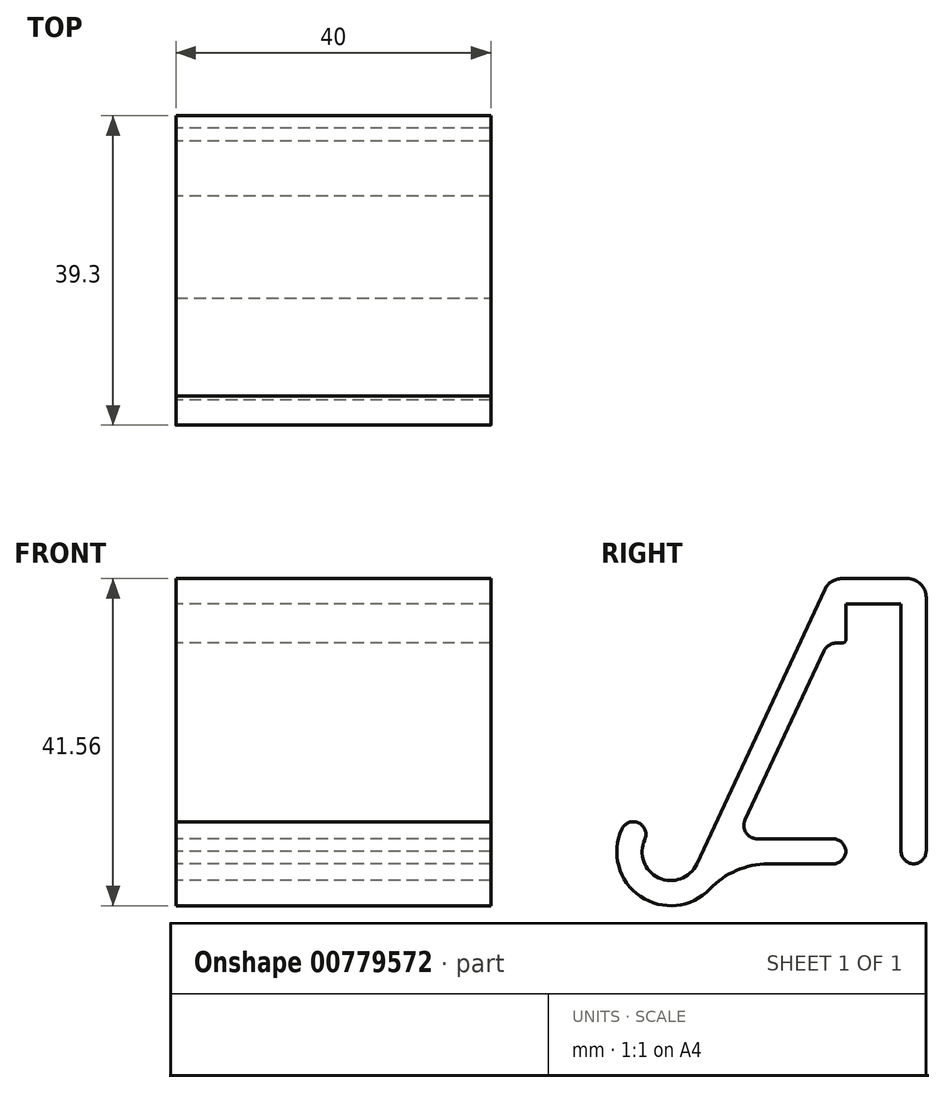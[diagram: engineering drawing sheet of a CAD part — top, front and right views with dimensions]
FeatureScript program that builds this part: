
annotation { "Feature Type Name" : "Feature", "Feature Type Description" : "" }
export const myFeature = defineFeature(function(context is Context, id is Id, definition is map)
    precondition{}
    {
        {
            var Q0;
            Q0=qCreatedBy(makeId("Right.planeOp"),FACE);
            var sketch = newSketch(context, id + "F0", { "sketchPlane" : qUnion([Q0])});
            skLineSegment(sketch, "E0", {"start": v(0, 0) * mm, "end": v(0, 33.05) * mm});
            skLineSegment(sketch, "E1", {"start": v(0, 33.05) * mm, "end": v(7, 33.05) * mm});
            skLineSegment(sketch, "E2", {"start": v(7, 33.05) * mm, "end": v(7, 0) * mm});
            skLineSegment(sketch, "E3", {"start": v(7, 0) * mm, "end": v(10.2, 0) * mm});
            skLineSegment(sketch, "E4", {"start": v(10.2, 0) * mm, "end": v(10.2, 36.25) * mm});
            skLineSegment(sketch, "E5", {"start": v(10.2, 36.25) * mm, "end": v(-2.04, 36.25) * mm});
            skLineSegment(sketch, "E6", {"start": v(-2.04, 36.25) * mm, "end": v(-2.04, 0) * mm, "construction": true});
            skLineSegment(sketch, "E7", {"start": v(-2.04, 0) * mm, "end": v(0, 0) * mm});
            skLineSegment(sketch, "E8", {"start": v(0, 33.05) * mm, "end": v(0, 36.25) * mm, "construction": true});
            skLineSegment(sketch, "E9", {"start": v(-2.04, 0) * mm, "end": v(-18.94, 0) * mm});
            skLineSegment(sketch, "E10", {"start": v(-18.94, 0) * mm, "end": v(-2.04, 36.25) * mm});
            skLineSegment(sketch, "E11", {"start": v(-18.94, 0) * mm, "end": v(-25.56, 3.09) * mm, "construction": true});
            skArc(sketch, "E12", {"start": v(-25.56, 3.09) * mm, "mid": v(-23.8, -1.77) * mm, "end": v(-18.94, 0) * mm});
            skLineSegment(sketch, "E13", {"start": v(-25.56, 3.09) * mm, "end": v(-28.46, 4.44) * mm, "construction": true});
            skCircle(sketch, "E14", {"center": v(-27, 3.76) * mm, "radius": 1.6 * mm});
            skCircle(sketch, "E15", {"center": v(-22.25, 1.54) * mm, "radius": 6.85 * mm});
            skLineSegment(sketch, "E16", {"start": v(-16.04, -1.35) * mm, "end": v(0, 33.05) * mm});
            skLineSegment(sketch, "E17", {"start": v(0, 33.05) * mm, "end": v(0, 33.05) * mm});
            skLineSegment(sketch, "E18", {"start": v(0, 3.2) * mm, "end": v(-17.45, 3.2) * mm});
            skLineSegment(sketch, "E19", {"start": v(-5.37, 3.2) * mm, "end": v(-5.37, 0) * mm, "construction": true});
            skLineSegment(sketch, "E20", {"start": v(0, 28.05) * mm, "end": v(-2.33, 28.05) * mm});
            skSolve(sketch);
        }
        {
            var Q0;
            {var subQ0=sQuery(id+"F0.wireOp",EDGE,"E14");var subQ1=makeQuery(id+"F0.imprint","INTERSECT",VERTEX,{"derivedFrom":[sQuery(id+"F0.wireOp",EDGE,"E12"),subQ0]});Q0=makeQuery(id+"F0.imprint","IMPRINT",FACE,{"disambiguationData":[TD([[makeQuery(id+"F0.imprint","IMPRINT",EDGE,{"disambiguationData":[TD([[subQ1,1.0]])],"derivedFrom":subQ0}),1.0]])]});}
            var Q1;
            {var subQ4=sQuery(id+"F0.wireOp",EDGE,"E12");Q1=makeQuery(id+"F0.imprint","IMPRINT",FACE,{"disambiguationData":[TD([[makeQuery(id+"F0.imprint","IMPRINT",EDGE,{"derivedFrom":subQ4}),-1.0]])]});}
            var Q2;
            {var subQ1=sQuery(id+"F0.wireOp",EDGE,"E9");var subQ3=sQuery(id+"F0.wireOp",EDGE,"E15");var subQ4=makeQuery(id+"F0.imprint","INTERSECT",VERTEX,{"derivedFrom":[subQ1,subQ3]});Q2=makeQuery(id+"F0.imprint","IMPRINT",FACE,{"disambiguationData":[TD([[makeQuery(id+"F0.imprint","IMPRINT",EDGE,{"disambiguationData":[TD([[subQ4,-1.0]])],"derivedFrom":subQ3}),1.0]])]});}
            var Q3;
            {var subQ0=sQuery(id+"F0.wireOp",EDGE,"E16");var subQ1=sQuery(id+"F0.wireOp",EDGE,"E9");var subQ2=makeQuery(id+"F0.imprint","INTERSECT",VERTEX,{"derivedFrom":[subQ1,subQ0]});Q3=makeQuery(id+"F0.imprint","IMPRINT",FACE,{"disambiguationData":[TD([[makeQuery(id+"F0.imprint","IMPRINT",EDGE,{"disambiguationData":[TD([[subQ2,-1.0]])],"derivedFrom":subQ1}),-1.0]])]});}
            var Q4;
            {var subQ5=sQuery(id+"F0.wireOp",EDGE,"E7");Q4=makeQuery(id+"F0.imprint","IMPRINT",FACE,{"disambiguationData":[TD([[makeQuery(id+"F0.imprint","IMPRINT",EDGE,{"derivedFrom":subQ5}),1.0]])]});}
            var Q5;
            Q5=makeQuery(id+"F0.imprint","IMPRINT",FACE,{"disambiguationData":[TD([[makeQuery(id+"F0.imprint","IMPRINT",EDGE,{"derivedFrom":sQuery(id+"F0.wireOp",EDGE,"E1")}),1.0]])]});
            var Q6;
            {var subQ0=sQuery(id+"F0.wireOp",EDGE,"E16");var subQ1=sQuery(id+"F0.wireOp",EDGE,"E9");var subQ2=makeQuery(id+"F0.imprint","INTERSECT",VERTEX,{"derivedFrom":[subQ1,subQ0]});Q6=makeQuery(id+"F0.imprint","IMPRINT",FACE,{"disambiguationData":[TD([[makeQuery(id+"F0.imprint","IMPRINT",EDGE,{"disambiguationData":[TD([[subQ2,-1.0]])],"derivedFrom":subQ1}),1.0]])]});}
            var Q7;
            {var subQ0=sQuery(id+"F0.wireOp",EDGE,"E18");var subQ1=sQuery(id+"F0.wireOp",EDGE,"E10");var subQ2=makeQuery(id+"F0.imprint","INTERSECT",VERTEX,{"derivedFrom":[subQ1,subQ0]});Q7=makeQuery(id+"F0.imprint","IMPRINT",FACE,{"disambiguationData":[TD([[makeQuery(id+"F0.imprint","IMPRINT",EDGE,{"disambiguationData":[TD([[subQ2,-1.0]])],"derivedFrom":subQ1}),-1.0]])]});}
            var Q8;
            {var subQ3=sQuery(id+"F0.wireOp",EDGE,"E20");Q8=makeQuery(id+"F0.imprint","IMPRINT",FACE,{"disambiguationData":[TD([[makeQuery(id+"F0.imprint","IMPRINT",EDGE,{"derivedFrom":subQ3}),-1.0]])]});}
            extrude(context, id + "F1", {"entities" : qUnion([Q0, Q1, Q2, Q3, Q4, Q5, Q6, Q7, Q8]), "depth" : 40 * mm, "offsetDistance" : 25 * mm});
        }
        {
            var Q0;
            Q0=makeQuery(id+"F1.opExtrude","SWEPT_EDGE",EDGE,{"disambiguationData":[OSD([sQuery(id+"F0.wireOp",EDGE,"E5"),sQuery(id+"F0.wireOp",EDGE,"E10")])]});
            var Q1;
            Q1=makeQuery(id+"F1.opExtrude","SWEPT_EDGE",EDGE,{"disambiguationData":[OSD([sQuery(id+"F0.wireOp",EDGE,"E4"),sQuery(id+"F0.wireOp",EDGE,"E5")])]});
            fillet(context, id + "F2", {"entities" : qUnion([Q0, Q1]), "radius" : 2.41 * mm, "tangentPropagation" : true, "allowEdgeOverflow" : false});
        }
        {
            var Q0;
            Q0=makeQuery(id+"F1.opExtrude","SWEPT_EDGE",EDGE,{"disambiguationData":[OSD([sQuery(id+"F0.wireOp",EDGE,"E9"),sQuery(id+"F0.wireOp",EDGE,"E16")])]});
            fillet(context, id + "F3", {"entities" : qUnion([Q0]), "radius" : 10.23 * mm, "tangentPropagation" : true, "allowEdgeOverflow" : false});
        }
        {
            var Q0;
            Q0=makeQuery(id+"F1.opExtrude","SWEPT_EDGE",EDGE,{"disambiguationData":[OSD([sQuery(id+"F0.wireOp",EDGE,"E16"),sQuery(id+"F0.wireOp",EDGE,"E18")])]});
            var Q1;
            Q1=makeQuery(id+"F1.opExtrude","SWEPT_EDGE",EDGE,{"disambiguationData":[OSD([sQuery(id+"F0.wireOp",EDGE,"E16"),sQuery(id+"F0.wireOp",EDGE,"E17")])]});
            var Q2;
            Q2=makeQuery(id+"F1.opExtrude","SWEPT_EDGE",EDGE,{"disambiguationData":[OSD([sQuery(id+"F0.wireOp",EDGE,"E2"),sQuery(id+"F0.wireOp",EDGE,"E3")])]});
            var Q3;
            Q3=makeQuery(id+"F1.opExtrude","SWEPT_EDGE",EDGE,{"disambiguationData":[OSD([sQuery(id+"F0.wireOp",EDGE,"E0"),sQuery(id+"F0.wireOp",EDGE,"E18")])]});
            var Q4;
            Q4=makeQuery(id+"F1.opExtrude","SWEPT_EDGE",EDGE,{"disambiguationData":[OSD([sQuery(id+"F0.wireOp",EDGE,"E0"),sQuery(id+"F0.wireOp",EDGE,"E7")])]});
            var Q5;
            Q5=makeQuery(id+"F1.opExtrude","SWEPT_EDGE",EDGE,{"disambiguationData":[OSD([sQuery(id+"F0.wireOp",EDGE,"E3"),sQuery(id+"F0.wireOp",EDGE,"E4")])]});
            fillet(context, id + "F4", {"entities" : qUnion([Q0, Q1, Q2, Q3, Q4, Q5]), "radius" : 1.69 * mm, "tangentPropagation" : true, "allowEdgeOverflow" : false});
        }
        {
            var Q0;
            Q0=makeQuery(id+"F1.opExtrude","SWEPT_EDGE",EDGE,{"disambiguationData":[OSD([sQuery(id+"F0.wireOp",EDGE,"E0"),sQuery(id+"F0.wireOp",EDGE,"E20")])]});
            fillet(context, id + "F5", {"entities" : qUnion([Q0]), "radius" : 0.5 * mm, "tangentPropagation" : true, "allowEdgeOverflow" : false});
        }
    });
